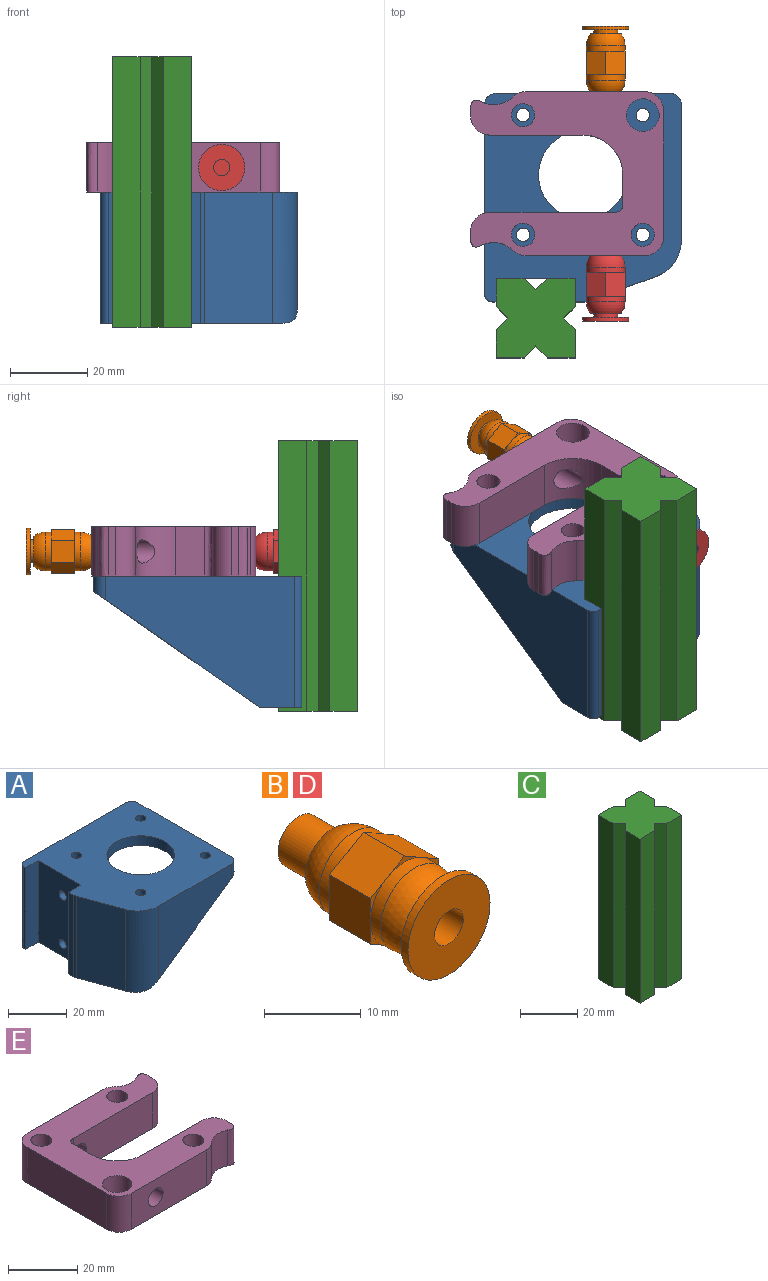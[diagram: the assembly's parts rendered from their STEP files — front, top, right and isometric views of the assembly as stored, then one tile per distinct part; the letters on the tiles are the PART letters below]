
ASSEMBLY  parts=5 mates=4
PART A: 35 faces, bbox 54x51x34 mm
  f0: plane 35.02x30.53mm, normal (0,-1,0), area 641.2mm2, adj f14,f18,f29,f33
  f1: plane 45x4mm, normal (1,0,0), area 180mm2, adj f6,f14,f33,f34
  f2: plane 49x34mm, normal (0,1,0), area 1107.9mm2, adj f14,f16,f17,f28,f34
  f3: plane 30.01x14.24mm, normal (0.94,0.34,0), area 454.4mm2, adj f6,f16,f27,f30,f31
  f4: plane 38.02x26.53mm, normal (0,1,0), area 504.3mm2, adj f6,f18,f31
  f5: plane 43x30mm, normal (0,-1,0), area 645mm2, adj f6,f17,f26
  f6: plane 49.94x45mm, normal (0,0,-1), area 1603.8mm2, adj f1,f3,f4,f5,f7,f15,f19,f20
  f7: plane 30x21.5mm, normal (1,0,0), area 625.8mm2, adj f6,f15,f16,f24,f25,f26
  f8: plane 34x1mm, normal (-1,0,0), area 34mm2, adj f9,f14,f16,f28
  f9: plane 34x6mm, normal (0,-1,0), area 204mm2, adj f8,f10,f14,f16
  f10: plane 34x20.5mm, normal (-1,0,0), area 677.8mm2, adj f9,f11,f14,f16,f24,f25
  f11: plane 34x6mm, normal (0,1,0), area 204mm2, adj f10,f12,f14,f16
  f12: plane 34x2.47mm, normal (-1,0,0), area 83.9mm2, adj f11,f14,f16,f32
  f13: plane 34x17.45mm, normal (-0.94,-0.34,0), area 632mm2, adj f14,f16,f29,f32
  f14: plane 54x51mm, normal (0,0,1), area 2053.2mm2, adj f0,f1,f2,f8,f9,f10,f11,f12
  f15: plane 30x2.94mm, normal (0,-1,0), area 88.2mm2, adj f6,f7,f16,f27
  f16: plane 46.83x11mm, normal (0,0,-1), area 177.3mm2, adj f2,f3,f7,f8,f9,f10,f11,f12
  f17: plane 43x30mm, normal (0.57,0,-0.82), area 154.9mm2, adj f2,f5,f16,f34
  f18: plane 40.45x28.23mm, normal (0.57,0,-0.82), area 145.6mm2, adj f0,f4,f29,f30,f31,f33
  f19: cylinder r=1.75mm len=4mm, axis (0,0,1), area 44mm2, adj f6,f14
  f20: cylinder r=1.75mm len=4mm, axis (0,0,1), area 44mm2, adj f6,f14
  f21: cylinder r=1.75mm len=4mm, axis (0,0,1), area 44mm2, adj f6,f14
  f22: cylinder r=1.75mm len=4mm, axis (0,0,1), area 44mm2, adj f6,f14
  f23: cylinder r=11.5mm len=23mm, axis (0,0,1), area 289mm2, adj f6,f14
  f24: cylinder r=1.75mm len=3.5mm, axis (1,0,0), area 33mm2, adj f7,f10
  f25: cylinder r=1.75mm len=3.5mm, axis (1,0,0), area 33mm2, adj f7,f10
  f26: cylinder r=2mm len=30mm, axis (0,0,1), area 94.2mm2, adj f5,f6,f7,f16
  f27: cylinder r=2mm len=30mm, axis (0,0,1), area 115.4mm2, adj f3,f6,f15,f16
  f28: cylinder r=2mm len=34mm, axis (0,0,-1), area 106.8mm2, adj f2,f8,f14,f16
  f29: cylinder r=10mm len=34mm, axis (0,0,1), area 404.4mm2, adj f0,f13,f14,f16,f18,f30
  f30: cylinder r=10mm len=11.52mm, axis (0,1,0), area 26.8mm2, adj f3,f16,f18,f29,f31
  f31: cylinder r=7mm len=29.88mm, axis (0,0,-1), area 245.4mm2, adj f3,f4,f6,f18,f30
  f32: cylinder r=3mm len=34mm, axis (0,0,-1), area 35.9mm2, adj f12,f13,f14,f16
  f33: cylinder r=3mm len=6.09mm, axis (0,0,-1), area 22.4mm2, adj f0,f1,f14,f18
  f34: cylinder r=3mm len=6.09mm, axis (0,0,1), area 22.4mm2, adj f1,f2,f14,f17
PART B: 36 faces, bbox 12x22x12 mm
  f0: cylinder r=5mm len=10mm, axis (0,-1,0), area 47.1mm2, adj f3,f20,f21,f22,f23,f24,f26
  f1: cylinder r=2.1mm len=4.2mm, axis (0,-1,0), area 19.8mm2, adj f4,f8
  f2: plane 8x8mm, normal (0,1,0), area 22mm2, adj f3,f7
  f3: sphere r=5mm, area 94.2mm2, adj f0,f2
  f4: plane 4.2x4.2mm, normal (0,-1,0), area 6.8mm2, adj f1,f5
  f5: cylinder r=1.5mm len=8mm, axis (0,-1,0), area 75.4mm2, adj f4,f6
  f6: plane 6x6mm, normal (0,1,0), area 21.2mm2, adj f5,f7
  f7: cylinder r=3mm len=6mm, axis (0,-1,0), area 94.2mm2, adj f2,f6
  f8: plane 4.2x4.2mm, normal (0,1,0), area 13.9mm2, adj f1
  f9: plane 6x5mm, normal (0.5,0,-0.87), area 34.6mm2, adj f10,f14,f15,f20,f25,f26
  f10: plane 6x5.77mm, normal (1,0,0), area 34.6mm2, adj f9,f11,f15,f16,f20,f21
  f11: plane 6x5mm, normal (0.5,0,0.87), area 34.6mm2, adj f10,f12,f16,f17,f21,f22
  f12: plane 6x5mm, normal (-0.5,0,0.87), area 34.6mm2, adj f11,f13,f17,f18,f22,f23
  f13: plane 6x5.77mm, normal (-1,0,0), area 34.6mm2, adj f12,f14,f18,f19,f23,f24
  f14: plane 6x5mm, normal (-0.5,0,-0.87), area 34.6mm2, adj f9,f13,f19,f24,f25,f26
  f15: plane 4.33x2.5mm, normal (0,-1,0), area 1.3mm2, adj f9,f10,f29
  f16: plane 4.33x2.5mm, normal (0,-1,0), area 1.3mm2, adj f10,f11,f29
  f17: plane 5x1.44mm, normal (0,-1,0), area 1.3mm2, adj f11,f12,f29
  f18: plane 4.33x2.5mm, normal (0,-1,0), area 1.3mm2, adj f12,f13,f29
  f19: plane 4.33x2.5mm, normal (0,-1,0), area 1.3mm2, adj f13,f14,f29
  f20: plane 4.33x2.5mm, normal (0,1,0), area 1.3mm2, adj f0,f9,f10
  f21: plane 4.33x2.5mm, normal (0,1,0), area 1.3mm2, adj f0,f10,f11
  f22: plane 5x1.44mm, normal (0,1,0), area 1.3mm2, adj f0,f11,f12
  f23: plane 4.33x2.5mm, normal (0,1,0), area 1.3mm2, adj f0,f12,f13
  f24: plane 4.33x2.5mm, normal (0,1,0), area 1.3mm2, adj f0,f13,f14
  f25: plane 5x1.44mm, normal (0,-1,0), area 1.3mm2, adj f9,f14,f29
  f26: plane 5x1.44mm, normal (0,1,0), area 1.3mm2, adj f0,f9,f14
  f27: plane 8x8mm, normal (0,-1,0), area 20.1mm2, adj f28,f30
  f28: sphere r=5mm, area 94.2mm2, adj f27,f29
  f29: cylinder r=5mm len=10mm, axis (0,-1,0), area 47.1mm2, adj f15,f16,f17,f18,f19,f25,f28
  f30: cylinder r=3.1mm len=6.2mm, axis (0,-1,0), area 19.5mm2, adj f27,f31
  f31: plane 12x12mm, normal (0,1,0), area 82.9mm2, adj f30,f32
  f32: cylinder r=6mm len=12mm, axis (0,-1,0), area 37.7mm2, adj f31,f33
  f33: plane 12x12mm, normal (0,-1,0), area 99.2mm2, adj f32,f35
  f34: plane 4.2x4.2mm, normal (0,-1,0), area 13.9mm2, adj f35
  f35: cylinder r=2.1mm len=6.5mm, axis (0,-1,0), area 85.8mm2, adj f33,f34
PART C: 18 faces, bbox 20.5x20.5x70 mm
  f0: plane 70x7.25mm, normal (0,-1,0), area 507.5mm2, adj f4,f5,f9,f17
  f1: plane 70x7.25mm, normal (1,0,0), area 507.5mm2, adj f4,f5,f8,f10
  f2: plane 70x7.25mm, normal (0,1,0), area 507.5mm2, adj f3,f4,f5,f12
  f3: plane 70x7.25mm, normal (-1,0,0), area 507.5mm2, adj f2,f4,f5,f15
  f4: plane 20.5x20.5mm, normal (0,0,1), area 384.3mm2, adj f0,f1,f2,f3,f6,f7,f8,f9
  f5: plane 20.5x20.5mm, normal (0,0,-1), area 384.3mm2, adj f0,f1,f2,f3,f6,f7,f8,f9
  f6: plane 70x7.25mm, normal (0,-1,0), area 507.5mm2, adj f4,f5,f7,f16
  f7: plane 70x7.25mm, normal (1,0,0), area 507.5mm2, adj f4,f5,f6,f11
  f8: plane 70x7.25mm, normal (0,1,0), area 507.5mm2, adj f1,f4,f5,f13
  f9: plane 70x7.25mm, normal (-1,0,0), area 507.5mm2, adj f0,f4,f5,f14
  f10: plane 70x3mm, normal (0.71,-0.71,0), area 297mm2, adj f1,f4,f5,f11
  f11: plane 70x3mm, normal (0.71,0.71,0), area 297mm2, adj f4,f5,f7,f10
  f12: plane 70x3mm, normal (0.71,0.71,0), area 297mm2, adj f2,f4,f5,f13
  f13: plane 70x3mm, normal (-0.71,0.71,0), area 297mm2, adj f4,f5,f8,f12
  f14: plane 70x3mm, normal (-0.71,0.71,0), area 297mm2, adj f4,f5,f9,f15
  f15: plane 70x3mm, normal (-0.71,-0.71,0), area 297mm2, adj f3,f4,f5,f14
  f16: plane 70x3mm, normal (-0.71,-0.71,0), area 297mm2, adj f4,f5,f6,f17
  f17: plane 70x3mm, normal (0.71,-0.71,0), area 297mm2, adj f0,f4,f5,f16
PART D: same geometry as B
PART E: 28 faces, bbox 50.2x42.7x14.2 mm
  f0: plane 30.64x12.7mm, normal (0,-1,0), area 360.8mm2, adj f13,f14,f18,f20,f24
  f1: plane 30.64x12.7mm, normal (0,1,0), area 360.8mm2, adj f13,f14,f17,f19,f23
  f2: plane 32.5x12.7mm, normal (-1,0,0), area 412.7mm2, adj f13,f14,f23,f24
  f3: plane 12.7x1.79mm, normal (1,0,0), area 22.8mm2, adj f13,f14,f22,f25
  f4: plane 24.1x12.7mm, normal (0,1,0), area 306.1mm2, adj f5,f13,f14,f22
  f5: cylinder r=10.35mm len=12.7mm, axis (0,0,-1), area 170.5mm2, adj f4,f6,f13,f14,f18
  f6: plane 12.7x7.65mm, normal (1,0,0), area 97.2mm2, adj f5,f13,f14,f27
  f7: plane 32.45x12.7mm, normal (0,-1,0), area 385.1mm2, adj f13,f14,f17,f21,f27
  f8: cylinder r=3mm len=12.7mm, axis (0,0,-1), area 239.4mm2, adj f13,f14
  f9: cylinder r=4.25mm len=12.7mm, axis (0,0,-1), area 339.1mm2, adj f13,f14
  f10: cylinder r=3mm len=12.7mm, axis (0,0,-1), area 239.4mm2, adj f13,f14
  f11: plane 12.7x1.79mm, normal (1,0,0), area 22.8mm2, adj f13,f14,f21,f26
  f12: cylinder r=3mm len=12.7mm, axis (0,0,-1), area 239.4mm2, adj f13,f14
  f13: plane 50.21x42.71mm, normal (0,0,1), area 1130.8mm2, adj f0,f1,f2,f3,f4,f5,f6,f7
  f14: plane 50.21x42.71mm, normal (0,0,-1), area 1130.8mm2, adj f0,f1,f2,f3,f4,f5,f6,f7
  f15: cylinder r=7mm len=12.7mm, axis (0,0,1), area 109.5mm2, adj f13,f14,f19,f26
  f16: cylinder r=7mm len=12.7mm, axis (0,0,1), area 109.5mm2, adj f13,f14,f20,f25
  f17: cylinder r=3mm len=11.25mm, axis (0,-1,0), area 212.1mm2, adj f1,f7,f27
  f18: cylinder r=3mm len=16.32mm, axis (0,-1,0), area 255mm2, adj f0,f5
  f19: cylinder r=5mm len=12.7mm, axis (0,0,1), area 49mm2, adj f1,f13,f14,f15
  f20: cylinder r=5mm len=12.7mm, axis (0,0,1), area 49mm2, adj f0,f13,f14,f16
  f21: cylinder r=5mm len=12.7mm, axis (0,0,-1), area 99.7mm2, adj f7,f11,f13,f14
  f22: cylinder r=5mm len=12.7mm, axis (0,0,-1), area 99.7mm2, adj f3,f4,f13,f14
  f23: cylinder r=5mm len=12.7mm, axis (0,0,1), area 99.7mm2, adj f1,f2,f13,f14
  f24: cylinder r=5mm len=12.7mm, axis (0,0,1), area 99.7mm2, adj f0,f2,f13,f14
  f25: bspline ~13.97x2.89mm, area 57.9mm2, adj f3,f13,f14,f16
  f26: bspline ~13.97x2.89mm, area 57.9mm2, adj f11,f13,f14,f15
  f27: bspline ~13.97x2mm, area 41.3mm2, adj f6,f7,f13,f14,f17
PLACE A rot(axis=(0,0,1),90deg) t=(-29.2,65.1,-0.16)mm
PLACE B rot(axis=(1,0,0),180deg) t=(-42.25,89.95,20.54)mm
PLACE C t=(-29.2,65.1,3.84)mm
PLACE D t=(-42.25,115.15,-0.16)mm
PLACE E rot(axis=(0,0,1),180deg) t=(20.15,89.95,-0.16)mm
MATE fastened B.f0 <-> E.f17  axis (0,-1,0) through (-11.05,123.8,10.19)mm
MATE fastened D.f0 <-> E.f17  axis (0,-1,0) through (-11.05,81.3,10.19)mm
MATE fastened A.f10 <-> C.f8  axis (0,-1,0) through (-18.95,75.35,3.84)mm
MATE fastened E.f9 <-> A.f21  axis (0,0,-1) through (-1.45,117.7,3.84)mm
